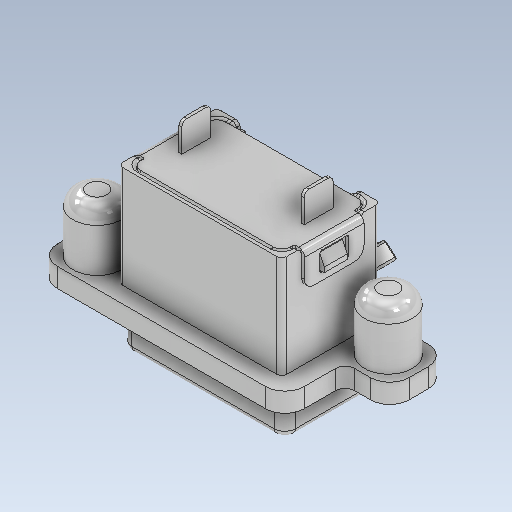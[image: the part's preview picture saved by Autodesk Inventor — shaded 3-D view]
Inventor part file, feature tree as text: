
AUTODESK INVENTOR PART (.ipt)
format: ipt  version: 2021 (Build 250183000, 183)  size: 1,382,912 bytes
history: native  units: mm
features: extrude x3, sketch x3, plane x1, fillet x1, imported_body x1
ambient origin geometry x8: Origin, YZ Plane, XZ Plane, XY Plane, X Axis, Y Axis, Z Axis, Center Point
bodies: Solid1 (feature_tree)
feature tree (9):
  extrude  "Extrusion1"  TaperAngle=0.0deg  [1 undecoded]
  extrude  "Extrusion2"  Depth=6.35mm
  sketch  "Sketch3"  dims[d6=3.0mm d7=0.3mm d8=-15.5mm d9=10.0mm d10=0.0mm d11=0.5mm]
  plane  "Work Plane1"
  extrude  "Extrusion3"  Depth=0.3mm
  fillet  "Fillet1"  [1 undecoded]
  sketch  "Sketch1"  dims[d0=0.0mm d1=0.0mm d2=0.0mm d3=0.0mm]
  sketch  "Sketch2"  dims[d4=4.4mm d5=6.35mm]
  imported_body  "Imported2"
note: 2 required parameter values undecoded (feature->parameter linkage not recoverable at this tier; creation-order binding heuristic only, values carry confidence <= 0.55)
